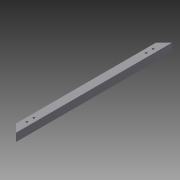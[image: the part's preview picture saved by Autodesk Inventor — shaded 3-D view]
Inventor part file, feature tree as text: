
AUTODESK INVENTOR PART (.ipt)
format: ipt  version: 2013 (Build 170138000, 138)  size: 111,104 bytes
history: native  units: in
note: dims shown in document units (in); Inventor stores cm internally (conversion verified against a paired STEP export)
features: reference x8, extrude x4, sketch x4
ambient origin geometry x8: Origin, YZ Plane, XZ Plane, XY Plane, X Axis, Y Axis, Z Axis, Center Point
bodies: Solid1 (feature_tree)
feature tree (16):
  extrude  "Extrusion1"  Depth=1.0in
  extrude  "Extrusion2"  Depth=19.5in TaperAngle=0.0deg
  extrude  "Extrusion3"  TaperAngle=45.0deg  [1 undecoded]
  extrude  "Extrusion4"  Depth=1.0in TaperAngle=0.0deg
  sketch  "Sketch1"  dims[d0=1.0in d2=1.0in]
  sketch  "Sketch2"  dims[d3=0.0625in d4=19.5in d5=0.0in]
  sketch  "Sketch3"  dims[d6=135.0deg d7=45.0deg]
  reference  "Reference1"
  reference  "Reference2"
  reference  "Reference3"
  reference  "Reference4"
  sketch  "Sketch4"  dims[d8=19.5in d9=0.0in d10=1.0in d11=0.0in d12=1.0in d13=0.0in]
  reference  "Reference5"
  reference  "Reference6"
  reference  "Reference7"
  reference  "Reference8"
note: 1 required parameter value undecoded (feature->parameter linkage not recoverable at this tier; creation-order binding heuristic only, values carry confidence <= 0.55)
